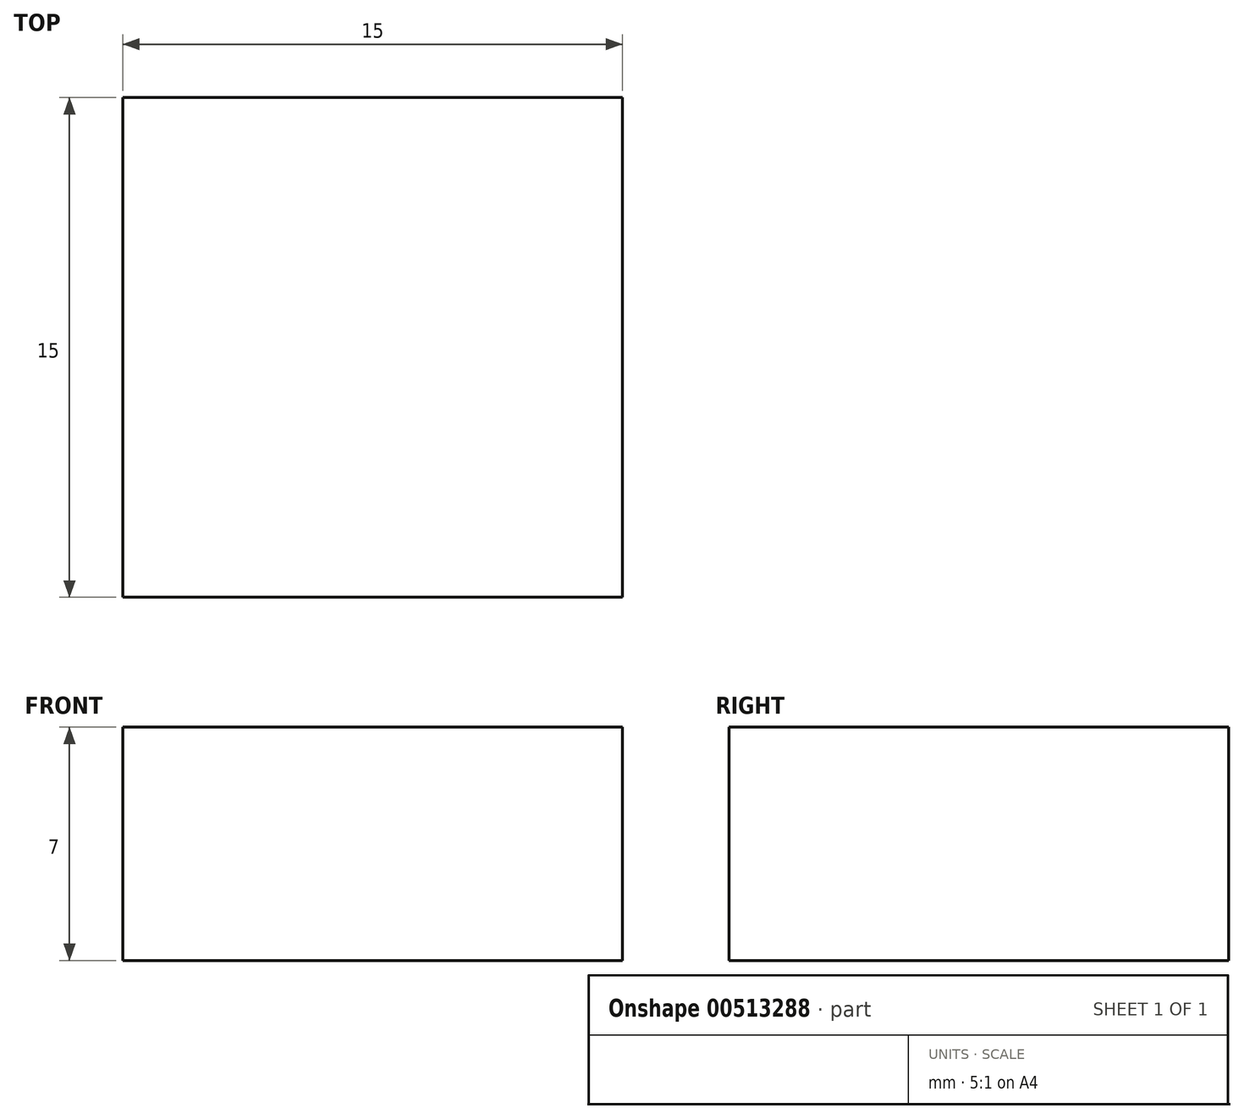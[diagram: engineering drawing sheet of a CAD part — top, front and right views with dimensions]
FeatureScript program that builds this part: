
annotation { "Feature Type Name" : "Feature", "Feature Type Description" : "" }
export const myFeature = defineFeature(function(context is Context, id is Id, definition is map)
    precondition{}
    {
        {
            var Q0;
            Q0=qCreatedBy(makeId("Top.planeOp"),FACE);
            var sketch = newSketch(context, id + "F0", { "sketchPlane" : qUnion([Q0])});
            skLineSegment(sketch, "E0.bottom", {"start": v(32.5, 25) * mm, "end": v(-32.5, 25) * mm});
            skLineSegment(sketch, "E0.top", {"start": v(32.5, -25) * mm, "end": v(-32.5, -25) * mm});
            skLineSegment(sketch, "E0.left", {"start": v(32.5, 25) * mm, "end": v(32.5, -25) * mm});
            skLineSegment(sketch, "E0.right", {"start": v(-32.5, 25) * mm, "end": v(-32.5, -25) * mm});
            skPoint(sketch, "E0.middle", {"position": v(0, 0) * mm});
            skLineSegment(sketch, "E1.bottom", {"start": v(-32.5, -25) * mm, "end": v(-17.5, -25) * mm});
            skLineSegment(sketch, "E1.top", {"start": v(-32.5, -10) * mm, "end": v(-17.5, -10) * mm});
            skLineSegment(sketch, "E1.left", {"start": v(-32.5, -25) * mm, "end": v(-32.5, -10) * mm});
            skLineSegment(sketch, "E1.right", {"start": v(-17.5, -25) * mm, "end": v(-17.5, -10) * mm});
            skLineSegment(sketch, "E2.bottom", {"start": v(-32.5, 25) * mm, "end": v(-17.5, 25) * mm});
            skLineSegment(sketch, "E2.top", {"start": v(-32.5, 10) * mm, "end": v(-17.5, 10) * mm});
            skLineSegment(sketch, "E2.left", {"start": v(-32.5, 25) * mm, "end": v(-32.5, 10) * mm});
            skLineSegment(sketch, "E2.right", {"start": v(-17.5, 25) * mm, "end": v(-17.5, 10) * mm});
            skSolve(sketch);
        }
        {
            var Q0;
            Q0=makeQuery(id+"F0.imprint","IMPRINT",FACE,{"disambiguationData":[TD([[makeQuery(id+"F0.imprint","IMPRINT",EDGE,{"derivedFrom":sQuery(id+"F0.wireOp",EDGE,"E0.bottom")}),1.0]])]});
            extrude(context, id + "F1", {"entities" : qUnion([Q0]), "depth" : 7 * mm});
        }
        {
            var Q0;
            Q0=makeQuery(id+"F1.opExtrude","SWEPT_FACE",FACE,{"disambiguationData":[OSD([sQuery(id+"F0.wireOp",EDGE,"E0.right")])]});
            var sketch = newSketch(context, id + "F2", { "sketchPlane" : qUnion([Q0])});
            skLineSegment(sketch, "E3", {"start": v(-10, 7) * mm, "end": v(10, 0) * mm});
            skPoint(sketch, "E4", {"position": v(0, 3.5) * mm});
            skPoint(sketch, "E5", {"position": v(-5, 3.5) * mm});
            skPoint(sketch, "E6", {"position": v(5, 3.5) * mm});
            skSolve(sketch);
        }
        {
            var Q0;
            Q0=sQuery(id+"F2.wireOp",VERTEX,"E5");
            var Q1;
            Q1=sQuery(id+"F2.wireOp",VERTEX,"E6");
            var Q2;
            Q2=makeQuery(id+"F1.opExtrude","SWEPT_BODY",BODY,{"disambiguationData":[OSD([sQuery(id+"F0.wireOp",EDGE,"E0.bottom"),sQuery(id+"F0.wireOp",EDGE,"E0.top"),sQuery(id+"F0.wireOp",EDGE,"E0.left"),sQuery(id+"F0.wireOp",EDGE,"E0.right"),sQuery(id+"F0.wireOp",EDGE,"E1.top"),sQuery(id+"F0.wireOp",EDGE,"E1.right"),sQuery(id+"F0.wireOp",EDGE,"E2.top"),sQuery(id+"F0.wireOp",EDGE,"E2.right")])]});
            hole(context, id + "F3", {"style" : HoleStyle.SIMPLE, "endStyle" : HoleEndStyle.BLIND, "holeDiameter" : 4 * mm, "holeDepth" : 6 * mm, "isTappedThrough" : true, "tappedDepth" : 12 * mm, "tapClearance" : 3, "locations" : qUnion([Q0, Q1]), "scope" : qUnion([Q2])});
        }
        {
            var Q0;
            Q0=makeQuery(id+"F1.opExtrude","CAP_FACE",FACE,{"disambiguationData":[OSD([sQuery(id+"F0.wireOp",EDGE,"E0.bottom"),sQuery(id+"F0.wireOp",EDGE,"E0.top"),sQuery(id+"F0.wireOp",EDGE,"E0.left"),sQuery(id+"F0.wireOp",EDGE,"E0.right"),sQuery(id+"F0.wireOp",EDGE,"E1.top"),sQuery(id+"F0.wireOp",EDGE,"E1.right"),sQuery(id+"F0.wireOp",EDGE,"E2.top"),sQuery(id+"F0.wireOp",EDGE,"E2.right")])],"isStart":false});
            var sketch = newSketch(context, id + "F4", { "sketchPlane" : qUnion([Q0])});
            skLineSegment(sketch, "E7.bottom", {"start": v(27.5, 6.3) * mm, "end": v(-10.1, 6.3) * mm});
            skLineSegment(sketch, "E7.top", {"start": v(27.5, -6.3) * mm, "end": v(-10.1, -6.3) * mm});
            skLineSegment(sketch, "E7.left", {"start": v(27.5, 6.3) * mm, "end": v(27.5, -6.3) * mm});
            skLineSegment(sketch, "E7.right", {"start": v(-10.1, 6.3) * mm, "end": v(-10.1, -6.3) * mm});
            skPoint(sketch, "E7.middle", {"position": v(8.7, 0) * mm});
            skSolve(sketch);
        }
        {
            var Q0;
            Q0=sQuery(id+"F4.wireOp",VERTEX,"E7.right.start");
            var Q1;
            Q1=sQuery(id+"F4.wireOp",VERTEX,"E7.right.end");
            var Q2;
            Q2=sQuery(id+"F4.wireOp",VERTEX,"E7.left.end");
            var Q3;
            Q3=sQuery(id+"F4.wireOp",VERTEX,"E7.bottom.start");
            var Q4;
            Q4=makeQuery(id+"F1.opExtrude","SWEPT_BODY",BODY,{"disambiguationData":[OSD([sQuery(id+"F0.wireOp",EDGE,"E0.bottom"),sQuery(id+"F0.wireOp",EDGE,"E0.top"),sQuery(id+"F0.wireOp",EDGE,"E0.left"),sQuery(id+"F0.wireOp",EDGE,"E0.right"),sQuery(id+"F0.wireOp",EDGE,"E1.top"),sQuery(id+"F0.wireOp",EDGE,"E1.right"),sQuery(id+"F0.wireOp",EDGE,"E2.top"),sQuery(id+"F0.wireOp",EDGE,"E2.right")])]});
            hole(context, id + "F5", {"style" : HoleStyle.C_BORE, "endStyle" : HoleEndStyle.THROUGH, "holeDiameter" : 4.2 * mm, "cBoreDiameter" : 8 * mm, "cBoreDepth" : 4 * mm, "isTappedThrough" : true, "tappedDepth" : 12 * mm, "tapClearance" : 3, "locations" : qUnion([Q0, Q1, Q2, Q3]), "scope" : qUnion([Q4])});
        }
    });
